# Revit family: QF_BPRO_CE 88-61_574892
name_source: partatom
category: Sonderausstattung
revit_build: Autodesk Revit 2018 (Build: 20190510_1515(x64)
units: mm (PartAtom-declared; Revit-internal decimal feet)

## family parameters
Arbeitsebenenbasiert = Nein
Beim Laden mit Abzugskörper schneiden = Nein
Bemaßung runder Anschluss = Durchmesser verwenden
Gemeinsam genutzt = Nein
Immer vertikal = Ja
Raumberechnungspunkt = Ja
Teiletyp = Normal

## types (1)
- CE 88-61
    Artikel Nummer = 574892
    Beschreibung = Bühnenspender, nicht beheizbar;
Plattform 881 x 611 mm
    Beschreibung durch Hersteller analog Leistungsverzeichniskurztext = Abmessungen

Länge:					1115 mm
Breite:					  730 mm 
Höhe:					  911 mm
Arbeitshöhe:					  900 mm


Ausführung

Aufbau
Der Bühnenspender besteht komplett aus CNS 18/10. Die Oberfläche ist mikroliert. 
Die Plattform dient zur Aufnahme unterschiedlicher Geschirrarten. Der Korpus ist einwandig und kompakt in geschlossener Ausführung aufgebaut.
Der Bühnenspender hat eine durchgehende pulverbeschichtete Innenverkleidung, um das Rutschen des Geschirrs und somit Beschädigungen an der Innenseite des Korpus zu vermeiden.
Durch Ein- bzw. Aushängen der Zugfedern kann die Federspannung entsprechend dem Stapelgut reguliert werden, um eine gleichbleibende Ausgabehöhe zu gewährleisten.
Bedienseitig ist ein CNS-Sicherheits-Schiebegriff mit seitlichen Stoßschutzelementen aus Kunststoff (Polyamid) angebracht.
Fahrbar ist der Spender mittels rostfreien Kunststoffrollen (4 Lenkrollen, 2 davon mit Feststeller mit 125 mm ø). Massive Stoßecken aus Kunststoff (Polyamid) an allen vier Ecken schützen vor Beschädigung.


Zubehör/ Optionen

•	Weitere Zubehöre und Rollenausführungen siehe Gesamt-Preisliste


Technische Daten

Werkstoff:		CNS 18/10
Gewicht:		77 kg 
Kapazität:		abhängig von Geschirrart
Lichtes Maß:		881 x 611 mm



Besonderheit

•	durchgehend pulverbeschichtete Innenverkleidung
•	Veränderung der Federspannung möglich
•	gemäß DIN 18665, Teil 6 


Fabrikat

Hersteller:			B.PRO
Modell:				CE 88/ 61
Best.Nr.			574 892
    Beschreibung durch Hersteller analog Leistungsverzeichnislangtext = Abmessungen

Länge:					1115 mm
Breite:					  730 mm 
Höhe:					  911 mm
Arbeitshöhe:					  900 mm


Ausführung

Aufbau
Der Bühnenspender besteht komplett aus CNS 18/10. Die Oberfläche ist mikroliert. 
Die Plattform dient zur Aufnahme unterschiedlicher Geschirrarten. Der Korpus ist einwandig und kompakt in geschlossener Ausführung aufgebaut.
Der Bühnenspender hat eine durchgehende pulverbeschichtete Innenverkleidung, um das Rutschen des Geschirrs und somit Beschädigungen an der Innenseite des Korpus zu vermeiden.
Durch Ein- bzw. Aushängen der Zugfedern kann die Federspannung entsprechend dem Stapelgut reguliert werden, um eine gleichbleibende Ausgabehöhe zu gewährleisten.
Bedienseitig ist ein CNS-Sicherheits-Schiebegriff mit seitlichen Stoßschutzelementen aus Kunststoff (Polyamid) angebracht.
Fahrbar ist der Spender mittels rostfreien Kunststoffrollen (4 Lenkrollen, 2 davon mit Feststeller mit 125 mm ø). Massive Stoßecken aus Kunststoff (Polyamid) an allen vier Ecken schützen vor Beschädigung.


Zubehör/ Optionen

•	Weitere Zubehöre und Rollenausführungen siehe Gesamt-Preisliste


Technische Daten

Werkstoff:		CNS 18/10
Gewicht:		77 kg 
Kapazität:		abhängig von Geschirrart
Lichtes Maß:		881 x 611 mm



Besonderheit

•	durchgehend pulverbeschichtete Innenverkleidung
•	Veränderung der Federspannung möglich
•	gemäß DIN 18665, Teil 6 


Fabrikat

Hersteller:			B.PRO
Modell:				CE 88/ 61
Best.Nr.			574 892
    Gerätegewicht Netto = 77.00 kg
    Großküchengerätezuordnung = Ja
    Hersteller = B.PRO GmbH
    Höhe = 911 mm  [stored 2.98885 ft]
    Höhe Korpus = 900 mm  [stored 2.95276 ft]
    Internetadresse Gerätehersteller = https://www.bpro-solutions.com
    Internetadresse für Ersatzteilliste = https://www.bpro-solutions.com
    Kosten = 2329.4 $
    Länge Gerätebreite = 1115 mm
    Länge Korpus = 1010 mm  [stored 3.31365 ft]
    Material = QF_Metal-Stainless-Steel_general
    Material_Stoßschutz = QF_Rubber-Black-Matt
    Modell = CE 88-61
    Plattform Länge = 881 mm  [stored 2.89042 ft]
    Plattform Tiefe = 611 mm  [stored 2.00459 ft]
    Schacht Tiefe = 600 mm
    Sockelhöhe = 161 mm  [stored 0.528215 ft]
    Tiefe = 730 mm
    Tiefe Korpus = 660 mm
    Typenkommentare = Bühnenspender, nicht beheizbar
    URL = https://www.bpro-solutions.com
    Warnhinweise = Ausführliche Gefahrenhinweise entnehmen Sie der Betriebsanleitung.
    Zubehör = Nein

note: [stored X ft] marks values corroborated as IEEE doubles in the binary element streams (Revit-internal decimal feet)
